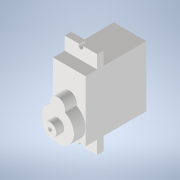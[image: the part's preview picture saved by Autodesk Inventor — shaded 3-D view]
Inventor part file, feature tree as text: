
AUTODESK INVENTOR PART (.ipt)
format: ipt  version: 2022 (Build 260153000, 153)  size: 170,496 bytes
history: native  units: mm
features: extrude x4, sketch x4, projected_geometry x3
ambient origin geometry x8: Origin, YZ Plane, XZ Plane, XY Plane, X Axis, Y Axis, Z Axis, Center Point
bodies: Solid1 (feature_tree)
feature tree (11):
  extrude  "Extrusion1"  Depth=4.3mm
  extrude  "Extrusion2"  Depth=15.8mm
  extrude  "Extrusion3"  Depth=4.9mm
  extrude  "Extrusion4"  Depth=2.9mm
  sketch  "Sketch1"  dims[d2=22.5mm d3=15.8mm d5=2.4mm d6=4.3mm d7=22.5mm d8=4.3mm]
  sketch  "Sketch2"  dims[d9=2.4mm d10=15.8mm]
  projected_geometry  "Projected Loop1"
  sketch  "Sketch3"  dims[d11=12.0mm d12=0.0mm d13=4.9mm]
  sketch  "Sketch4"  dims[d14=4.9mm d16=1.4mm d17=4.8mm d20=5.5mm d21=6.0mm d22=6.2mm d23=4.3mm d24=0.0mm d25=1.4mm d26=4.8mm d30=2.9mm d31=0.0mm d32=5.3mm d33=5.3mm d35=0.9mm d36=2.9mm d37=0.0mm]
  projected_geometry  "Projected Loop2"
  projected_geometry  "Projected Loop3"
